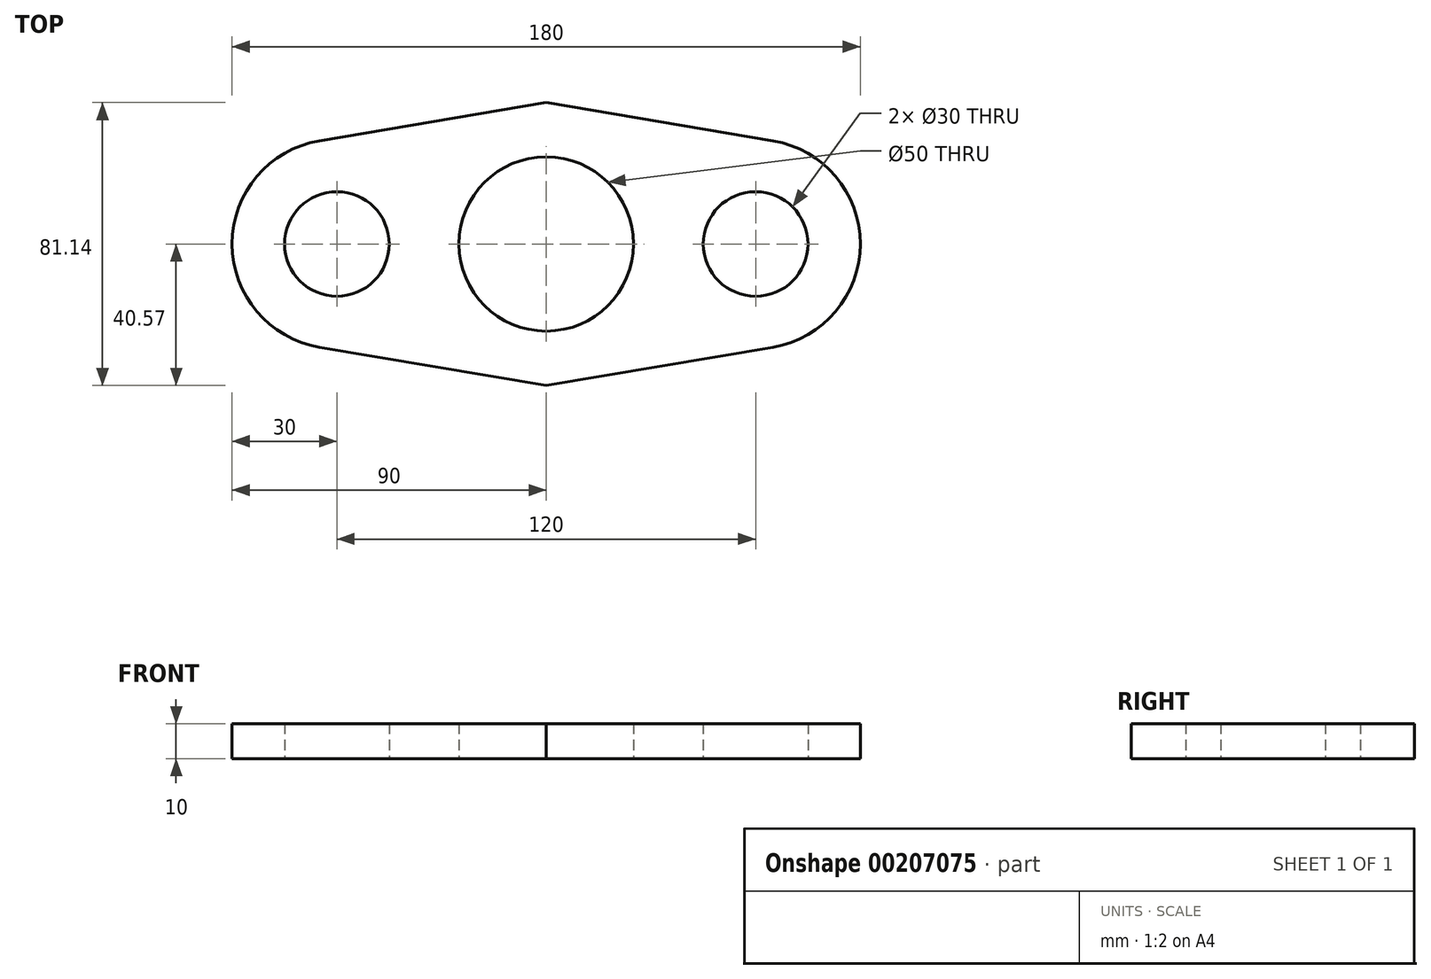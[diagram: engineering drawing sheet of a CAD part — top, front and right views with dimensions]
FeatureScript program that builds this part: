
annotation { "Feature Type Name" : "Feature", "Feature Type Description" : "" }
export const myFeature = defineFeature(function(context is Context, id is Id, definition is map)
    precondition{}
    {
        {
            var Q0;
            Q0=qCreatedBy(makeId("Top.planeOp"),FACE);
            var sketch = newSketch(context, id + "F0", { "sketchPlane" : qUnion([Q0])});
            skCircle(sketch, "E0", {"center": v(0, 0) * mm, "radius": 25 * mm});
            skCircle(sketch, "E1", {"center": v(60, 0) * mm, "radius": 15 * mm});
            skArc(sketch, "E2", {"start": v(65, -29.58) * mm, "mid": v(90, 0) * mm, "end": v(65, 29.58) * mm});
            skArc(sketch, "E3", {"start": v(-65, 29.58) * mm, "mid": v(-90, 0) * mm, "end": v(-65, -29.58) * mm});
            skCircle(sketch, "E4", {"center": v(-60, 0) * mm, "radius": 15 * mm});
            skLineSegment(sketch, "E5", {"start": v(-65, 29.58) * mm, "end": v(0, 40.57) * mm});
            skLineSegment(sketch, "E6", {"start": v(-65, -29.58) * mm, "end": v(0, -40.57) * mm});
            skLineSegment(sketch, "E7", {"start": v(0, -40.57) * mm, "end": v(65, -29.58) * mm});
            skPoint(sketch, "E8.orphan", {"position": v(0, 40.57) * mm});
            skLineSegment(sketch, "E9.trimOffspring", {"start": v(0, 40.57) * mm, "end": v(65, 29.58) * mm});
            skSolve(sketch);
        }
        {
            var Q0;
            Q0=makeQuery(id+"F0.imprint","IMPRINT",FACE,{"disambiguationData":[TD([[makeQuery(id+"F0.imprint","IMPRINT",EDGE,{"derivedFrom":sQuery(id+"F0.wireOp",EDGE,"E0")}),-1.0]])]});
            extrude(context, id + "F1", {"entities" : qUnion([Q0]), "depth" : 10 * mm});
        }
    });
